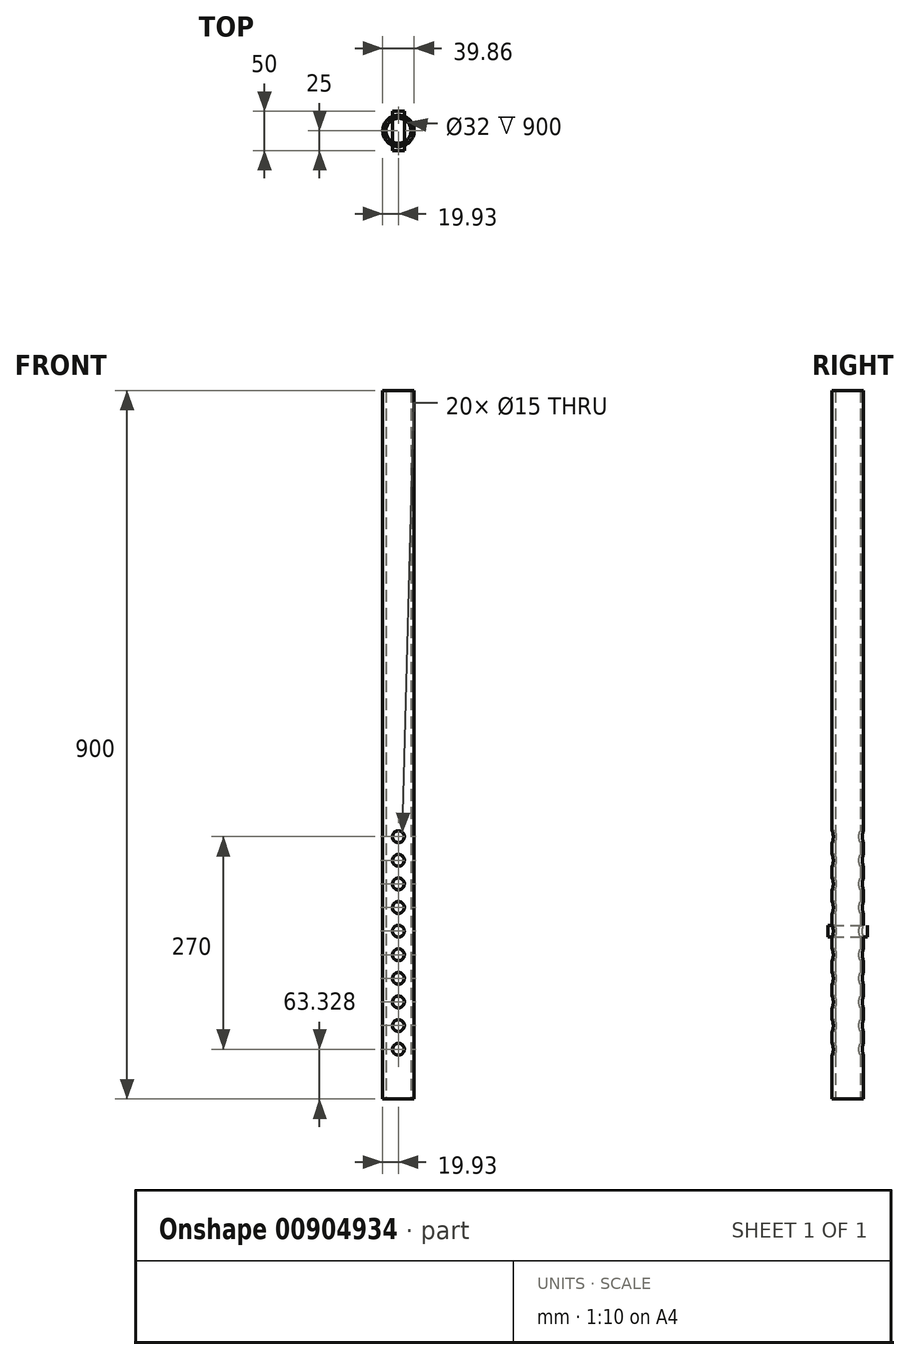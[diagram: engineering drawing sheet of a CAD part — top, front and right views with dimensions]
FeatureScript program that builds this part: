
annotation { "Feature Type Name" : "Feature", "Feature Type Description" : "" }
export const myFeature = defineFeature(function(context is Context, id is Id, definition is map)
    precondition{}
    {
        {
            var Q0;
            Q0=qCreatedBy(makeId("Top.planeOp"),FACE);
            var sketch = newSketch(context, id + "F0", { "sketchPlane" : qUnion([Q0])});
            skCircle(sketch, "E0", {"center": v(0, 0) * mm, "radius": 16 * mm});
            skCircle(sketch, "E1", {"center": v(0, 0) * mm, "radius": 19.93 * mm});
            skSolve(sketch);
        }
        {
            var Q0;
            Q0=qSketchRegion(id+"F0",true);
            extrude(context, id + "F1", {"entities" : qUnion([Q0]), "depth" : 900 * mm, "offsetDistance" : 25 * mm});
        }
        {
            var Q0;
            Q0=qCreatedBy(makeId("Front.planeOp"),FACE);
            var sketch = newSketch(context, id + "F2", { "sketchPlane" : qUnion([Q0])});
            skCircle(sketch, "E2", {"center": v(0, 63.33) * mm, "radius": 7.5 * mm});
            skCircle(sketch, "E3.1.0.0", {"center": v(0, 93.33) * mm, "radius": 7.5 * mm});
            skCircle(sketch, "E3.2.0.0", {"center": v(0, 123.33) * mm, "radius": 7.5 * mm});
            skLineSegment(sketch, "E3.direction1", {"start": v(0, 63.33) * mm, "end": v(0, 93.33) * mm, "construction": true});
            skCircle(sketch, "E4.0.3.0", {"center": v(0, 153.33) * mm, "radius": 7.5 * mm});
            skCircle(sketch, "E4.0.4.0", {"center": v(0, 183.33) * mm, "radius": 7.5 * mm});
            skCircle(sketch, "E4.0.5.0", {"center": v(0, 213.33) * mm, "radius": 7.5 * mm});
            skCircle(sketch, "E4.0.6.0", {"center": v(0, 243.33) * mm, "radius": 7.5 * mm});
            skCircle(sketch, "E4.0.7.0", {"center": v(0, 273.33) * mm, "radius": 7.5 * mm});
            skCircle(sketch, "E4.0.8.0", {"center": v(0, 303.33) * mm, "radius": 7.5 * mm});
            skCircle(sketch, "E4.0.9.0", {"center": v(0, 333.33) * mm, "radius": 7.5 * mm});
            skSolve(sketch);
        }
        {
            var Q0;
            Q0=qSketchRegion(id+"F2",true);
            extrude(context, id + "F3", {"entities" : qUnion([Q0]), "operationType" : NewBodyOperationType.REMOVE, "oppositeDirection" : true, "depth" : 60 * mm, "offsetDistance" : 25 * mm, "symmetric" : true});
        }
        {
            var Q0;
            Q0=qCreatedBy(makeId("Front.planeOp"),FACE);
            var sketch = newSketch(context, id + "F4", { "sketchPlane" : qUnion([Q0])});
            skCircle(sketch, "E5", {"center": v(0, 213.38) * mm, "radius": 7.5 * mm});
            skSolve(sketch);
        }
        {
            var Q0;
            Q0=qSketchRegion(id+"F4",true);
            extrude(context, id + "F5", {"entities" : qUnion([Q0]), "depth" : 50 * mm, "offsetDistance" : 25 * mm, "symmetric" : true});
        }
    });
